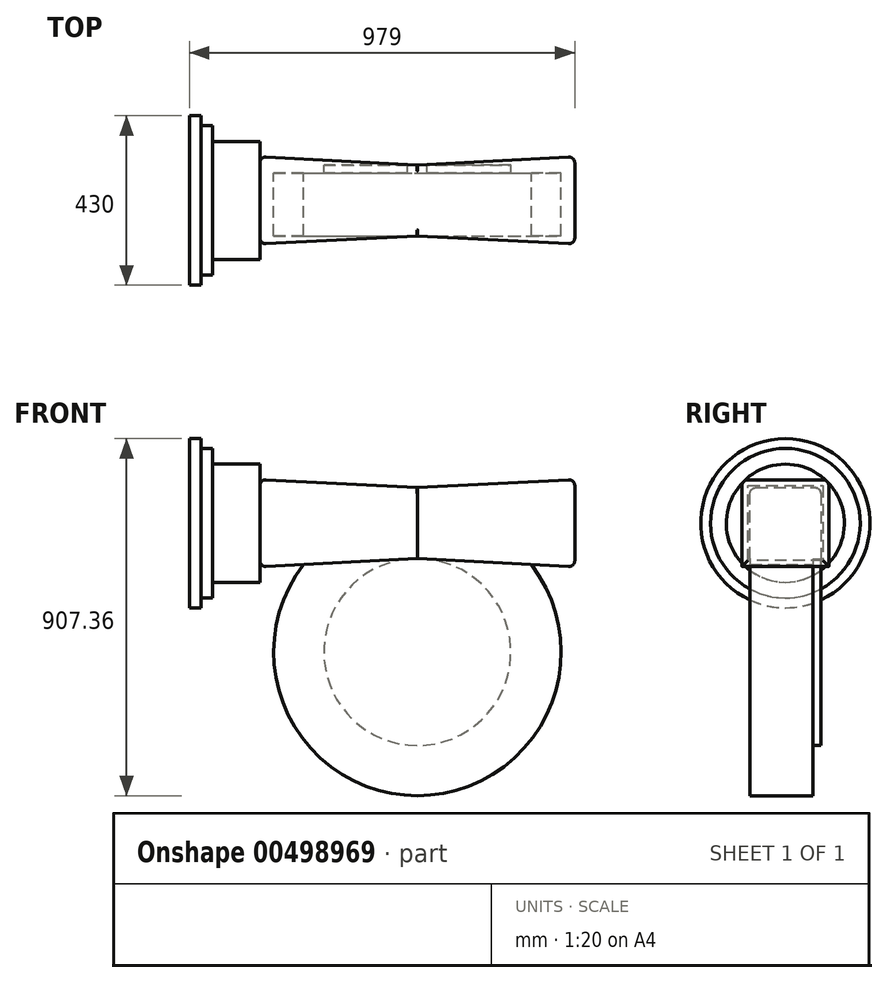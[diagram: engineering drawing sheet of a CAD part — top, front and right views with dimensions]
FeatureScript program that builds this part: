
annotation { "Feature Type Name" : "Feature", "Feature Type Description" : "" }
export const myFeature = defineFeature(function(context is Context, id is Id, definition is map)
    precondition{}
    {
        {
            var Q0;
            Q0=qCreatedBy(makeId("Front.planeOp"),FACE);
            var sketch = newSketch(context, id + "F0", { "sketchPlane" : qUnion([Q0])});
            skCircle(sketch, "E0", {"center": v(0, 0) * mm, "radius": 237.5 * mm});
            skSolve(sketch);
        }
        {
            var Q0;
            Q0 = qSketchRegion(id + "F0", true);
            extrude(context, id + "F1", {"entities" : qUnion([Q0]), "depth" : 20 * mm, "offsetDistance" : 25 * mm});
        }
        {
            var Q0;
            Q0=makeQuery(id+"F1.opExtrude","CAP_FACE",FACE,{"disambiguationData":[OSD([sQuery(id+"F0.wireOp",EDGE,"E0")])],"isStart":false});
            var sketch = newSketch(context, id + "F2", { "sketchPlane" : qUnion([Q0])});
            skLineSegment(sketch, "E1", {"start": v(-277.16, 237.5) * mm, "end": v(277.16, 237.5) * mm});
            skArc(sketch, "E2", {"start": v(-277.16, 237.5) * mm, "mid": v(0, -365) * mm, "end": v(277.16, 237.5) * mm});
            skSolve(sketch);
        }
        {
            var Q0;
            Q0 = qSketchRegion(id + "F2", true);
            extrude(context, id + "F3", {"entities" : qUnion([Q0]), "operationType" : NewBodyOperationType.ADD, "depth" : 160 * mm, "offsetDistance" : 25 * mm});
        }
        {
            var Q0;
            Q0=qCreatedBy(makeId("Right.planeOp"),FACE);
            var sketch = newSketch(context, id + "F4", { "sketchPlane" : qUnion([Q0])});
            skLineSegment(sketch, "E3.bottom", {"start": v(0, 417.5) * mm, "end": v(-180, 417.5) * mm});
            skLineSegment(sketch, "E3.top", {"start": v(0, 237.5) * mm, "end": v(-180, 237.5) * mm});
            skLineSegment(sketch, "E3.left", {"start": v(0, 417.5) * mm, "end": v(0, 237.5) * mm});
            skLineSegment(sketch, "E3.right", {"start": v(-180, 417.5) * mm, "end": v(-180, 237.5) * mm});
            skSolve(sketch);
        }
        {
            var Q0;
            Q0 = qSketchRegion(id + "F4", true);
            extrude(context, id + "F5", {"entities" : qUnion([Q0]), "operationType" : NewBodyOperationType.ADD, "endBound" : BoundingType.SYMMETRIC, "depth" : 800 * mm, "offsetDistance" : 25 * mm, "hasDraft" : true, "draftAngle" : 3 * degree});
        }
        {
            var Q0;
            Q0=makeQuery(id+"F5.*.split.splitOp","SPLIT",EDGE,{"derivedFrom":makeQuery(id+"F5.opExtrude","SWEPT_EDGE",EDGE,{"disambiguationData":[OSD([sQuery(id+"F4.wireOp",EDGE,"E3.bottom"),sQuery(id+"F4.wireOp",EDGE,"E3.left")])]})});
            var Q1;
            Q1=makeQuery(id+"F5.*.split.splitOp","SPLIT",EDGE,{"derivedFrom":makeQuery(id+"F5.opExtrude","SWEPT_EDGE",EDGE,{"disambiguationData":[OSD([sQuery(id+"F4.wireOp",EDGE,"E3.bottom"),sQuery(id+"F4.wireOp",EDGE,"E3.left")])]}),"isFromBackBody":true});
            var Q2;
            Q2=makeQuery(id+"F5.*.split.splitOp","SPLIT",FACE,{"derivedFrom":makeQuery(id+"F5.opExtrude","SWEPT_FACE",FACE,{"disambiguationData":[OSD([sQuery(id+"F4.wireOp",EDGE,"E3.bottom")])]}),"isFromBackBody":true});
            var Q3;
            Q3=makeQuery(id+"F5.*.split.splitOp","SPLIT",EDGE,{"derivedFrom":makeQuery(id+"F5.opExtrude","SWEPT_EDGE",EDGE,{"disambiguationData":[OSD([sQuery(id+"F4.wireOp",EDGE,"E3.bottom"),sQuery(id+"F4.wireOp",EDGE,"E3.right")])]})});
            var Q4;
            Q4=makeQuery(id+"F5.opExtrude","CAP_FACE",FACE,{"disambiguationData":[OSD([sQuery(id+"F4.wireOp",EDGE,"E3.bottom"),sQuery(id+"F4.wireOp",EDGE,"E3.top"),sQuery(id+"F4.wireOp",EDGE,"E3.left"),sQuery(id+"F4.wireOp",EDGE,"E3.right")])],"isStart":false});
            var Q5;
            Q5=makeQuery(id+"F5.opExtrude","CAP_FACE",FACE,{"disambiguationData":[OSD([sQuery(id+"F4.wireOp",EDGE,"E3.bottom"),sQuery(id+"F4.wireOp",EDGE,"E3.top"),sQuery(id+"F4.wireOp",EDGE,"E3.left"),sQuery(id+"F4.wireOp",EDGE,"E3.right")])],"isStart":true});
            fillet(context, id + "F6", {"entities" : qUnion([Q0, Q1, Q2, Q3, Q4, Q5]), "radius" : 15 * mm, "tangentPropagation" : true, "allowEdgeOverflow" : false});
        }
        {
            var Q0;
            Q0=makeQuery(id+"F5.opExtrude","CAP_FACE",FACE,{"disambiguationData":[OSD([sQuery(id+"F4.wireOp",EDGE,"E3.bottom"),sQuery(id+"F4.wireOp",EDGE,"E3.top"),sQuery(id+"F4.wireOp",EDGE,"E3.left"),sQuery(id+"F4.wireOp",EDGE,"E3.right")])],"isStart":true});
            var sketch = newSketch(context, id + "F7", { "sketchPlane" : qUnion([Q0])});
            skCircle(sketch, "E4", {"center": v(90.14, 327.36) * mm, "radius": 150 * mm});
            skSolve(sketch);
        }
        {
            var Q0;
            Q0 = qSketchRegion(id + "F7", true);
            extrude(context, id + "F8", {"entities" : qUnion([Q0]), "operationType" : NewBodyOperationType.ADD, "depth" : 120 * mm, "offsetDistance" : 25 * mm});
        }
        {
            var Q0;
            Q0=makeQuery(id+"F8.opExtrude","CAP_FACE",FACE,{"disambiguationData":[OSD([sQuery(id+"F7.wireOp",EDGE,"E4")])],"isStart":false});
            var sketch = newSketch(context, id + "F9", { "sketchPlane" : qUnion([Q0])});
            skCircle(sketch, "E5", {"center": v(90.14, 327.36) * mm, "radius": 190 * mm});
            skSolve(sketch);
        }
        {
            var Q0;
            Q0 = qSketchRegion(id + "F9", true);
            extrude(context, id + "F10", {"entities" : qUnion([Q0]), "operationType" : NewBodyOperationType.ADD, "depth" : 29 * mm, "offsetDistance" : 25 * mm});
        }
        {
            var Q0;
            Q0 = qSketchRegion(id + "F9", true);
            extrude(context, id + "F11", {"entities" : qUnion([Q0]), "operationType" : NewBodyOperationType.ADD, "depth" : 25 * mm, "offsetDistance" : 25 * mm});
        }
        {
            var Q0;
            Q0=makeQuery(id+"F10.opExtrude","CAP_FACE",FACE,{"disambiguationData":[OSD([sQuery(id+"F9.wireOp",EDGE,"E5")])],"isStart":false});
            var sketch = newSketch(context, id + "F12", { "sketchPlane" : qUnion([Q0])});
            skCircle(sketch, "E6", {"center": v(90.14, 327.36) * mm, "radius": 215 * mm});
            skSolve(sketch);
        }
        {
            var Q0;
            Q0 = qSketchRegion(id + "F12", true);
            extrude(context, id + "F13", {"entities" : qUnion([Q0]), "operationType" : NewBodyOperationType.ADD, "depth" : 30 * mm, "offsetDistance" : 25 * mm});
        }
    });
